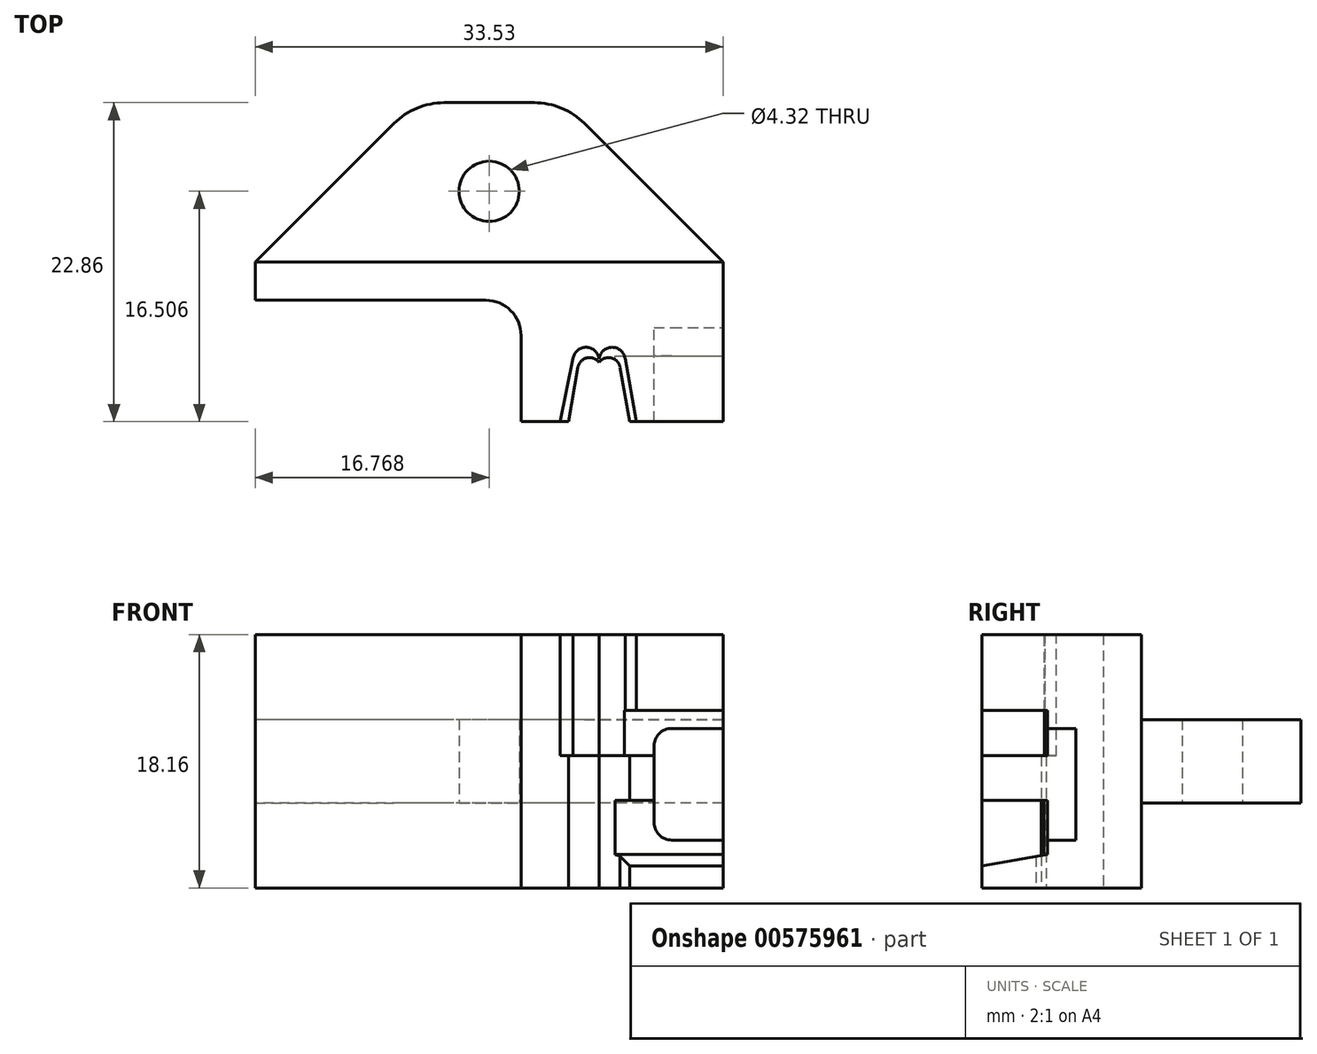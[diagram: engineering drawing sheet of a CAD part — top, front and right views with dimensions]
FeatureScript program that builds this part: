
annotation { "Feature Type Name" : "Feature", "Feature Type Description" : "" }
export const myFeature = defineFeature(function(context is Context, id is Id, definition is map)
    precondition{}
    {
        {
            var Q0;
            Q0=qCreatedBy(makeId("Top.planeOp"),FACE);
            var sketch = newSketch(context, id + "F0", { "sketchPlane" : qUnion([Q0])});
            skLineSegment(sketch, "E0.bottom", {"start": v(-12.43, 17.35) * mm, "end": v(21.1, 17.35) * mm});
            skLineSegment(sketch, "E0.top", {"start": v(-12.43, 5.92) * mm, "end": v(21.1, 5.92) * mm});
            skLineSegment(sketch, "E0.left", {"start": v(-12.43, 17.35) * mm, "end": v(-12.43, 5.92) * mm});
            skLineSegment(sketch, "E0.right", {"start": v(21.1, 17.35) * mm, "end": v(21.1, 5.92) * mm});
            skLineSegment(sketch, "E1.bottom", {"start": v(6.62, 5.92) * mm, "end": v(-9.89, 5.92) * mm});
            skLineSegment(sketch, "E1.top", {"start": v(6.62, 12.27) * mm, "end": v(-9.89, 12.27) * mm});
            skLineSegment(sketch, "E1.left", {"start": v(6.62, 5.92) * mm, "end": v(6.62, 12.27) * mm});
            skLineSegment(sketch, "E1.right", {"start": v(-9.89, 5.92) * mm, "end": v(-9.89, 12.27) * mm});
            skSolve(sketch);
        }
        {
            var Q0;
            Q0=makeQuery(id+"F0.imprint","IMPRINT",FACE,{"disambiguationData":[TD([[makeQuery(id+"F0.imprint","IMPRINT",EDGE,{"derivedFrom":sQuery(id+"F0.wireOp",EDGE,"E0.bottom")}),-1.0]])]});
            extrude(context, id + "F1", {"entities" : qUnion([Q0]), "depth" : 16.38 * mm, "offsetDistance" : 25.4 * mm});
        }
        {
            var Q0;
            Q0=makeQuery(id+"F1.opExtrude","SWEPT_FACE",FACE,{"disambiguationData":[OSD([sQuery(id+"F0.wireOp",EDGE,"E0.bottom")])]});
            var sketch = newSketch(context, id + "F2", { "sketchPlane" : qUnion([Q0])});
            skLineSegment(sketch, "E2.bottom", {"start": v(-21.1, 11.18) * mm, "end": v(12.43, 11.18) * mm});
            skLineSegment(sketch, "E2.top", {"start": v(-21.1, 5.2) * mm, "end": v(12.43, 5.2) * mm});
            skLineSegment(sketch, "E2.left", {"start": v(-21.1, 11.18) * mm, "end": v(-21.1, 5.2) * mm});
            skLineSegment(sketch, "E2.right", {"start": v(12.43, 11.18) * mm, "end": v(12.43, 5.2) * mm});
            skSolve(sketch);
        }
        {
            var Q0;
            Q0=makeQuery(id+"F2.imprint","IMPRINT",FACE,{"disambiguationData":[TD([[makeQuery(id+"F2.imprint","IMPRINT",EDGE,{"derivedFrom":sQuery(id+"F2.wireOp",EDGE,"E2.bottom")}),-1.0]])]});
            extrude(context, id + "F3", {"entities" : qUnion([Q0]), "operationType" : NewBodyOperationType.ADD, "depth" : 11.43 * mm, "offsetDistance" : 25.4 * mm});
        }
        {
            var Q0;
            Q0=makeQuery(id+"F3.opExtrude","CAP_EDGE",EDGE,{"disambiguationData":[OSD([sQuery(id+"F2.wireOp",EDGE,"E2.right")])],"isStart":false});
            var Q1;
            Q1=makeQuery(id+"F3.opExtrude","CAP_EDGE",EDGE,{"disambiguationData":[OSD([sQuery(id+"F2.wireOp",EDGE,"E2.left")])],"isStart":false});
            chamfer(context, id + "F4", {"entities" : qUnion([Q0, Q1]), "width" : 11.43 * mm, "tangentPropagation" : true});
        }
        {
            var Q0;
            Q0=makeQuery(id+"F3.opExtrude","SWEPT_FACE",FACE,{"disambiguationData":[OSD([sQuery(id+"F2.wireOp",EDGE,"E2.top")])]});
            var sketch = newSketch(context, id + "F5", { "sketchPlane" : qUnion([Q0])});
            skCircle(sketch, "E3", {"center": v(4.34, -22.43) * mm, "radius": 2.16 * mm});
            skSolve(sketch);
        }
        {
            var Q0;
            Q0=makeQuery(id+"F5.imprint","IMPRINT",FACE,{"disambiguationData":[TD([[makeQuery(id+"F5.imprint","IMPRINT",EDGE,{"derivedFrom":sQuery(id+"F5.wireOp",EDGE,"E3")}),1.0]])]});
            extrude(context, id + "F6", {"entities" : qUnion([Q0]), "operationType" : NewBodyOperationType.REMOVE, "oppositeDirection" : true, "depth" : 25.4 * mm, "offsetDistance" : 25.4 * mm});
        }
        {
            var Q0;
            Q0=makeQuery(id+"F1.opExtrude","CAP_FACE",FACE,{"disambiguationData":[OSD([sQuery(id+"F0.wireOp",EDGE,"E0.bottom"),sQuery(id+"F0.wireOp",EDGE,"E0.top"),sQuery(id+"F0.wireOp",EDGE,"E0.left"),sQuery(id+"F0.wireOp",EDGE,"E0.right")])],"isStart":true});
            var sketch = newSketch(context, id + "F7", { "sketchPlane" : qUnion([Q0])});
            skLineSegment(sketch, "E4", {"start": v(10.02, -5.92) * mm, "end": v(14.4, -5.92) * mm});
            skArc(sketch, "E5", {"start": v(12.21, -10.17) * mm, "mid": v(13.08, -10.5) * mm, "end": v(13.72, -9.82) * mm});
            skArc(sketch, "E6", {"start": v(10.7, -9.82) * mm, "mid": v(11.35, -10.5) * mm, "end": v(12.21, -10.17) * mm});
            skLineSegment(sketch, "E7", {"start": v(10.02, -5.92) * mm, "end": v(10.7, -9.82) * mm});
            skLineSegment(sketch, "E8", {"start": v(14.4, -5.92) * mm, "end": v(13.72, -9.82) * mm});
            skSolve(sketch);
        }
        {
            var Q0;
            Q0=makeQuery(id+"F7.imprint","IMPRINT",FACE,{"disambiguationData":[TD([[makeQuery(id+"F7.imprint","IMPRINT",EDGE,{"derivedFrom":sQuery(id+"F7.wireOp",EDGE,"E4")}),-1.0]])]});
            extrude(context, id + "F8", {"entities" : qUnion([Q0]), "operationType" : NewBodyOperationType.REMOVE, "oppositeDirection" : true, "depth" : 12.06 * mm, "offsetDistance" : 25.4 * mm});
        }
        {
            var Q0;
            Q0=makeQuery(id+"F1.opExtrude","CAP_FACE",FACE,{"disambiguationData":[OSD([sQuery(id+"F0.wireOp",EDGE,"E0.bottom"),sQuery(id+"F0.wireOp",EDGE,"E0.top"),sQuery(id+"F0.wireOp",EDGE,"E0.left"),sQuery(id+"F0.wireOp",EDGE,"E0.right")])],"isStart":false});
            var sketch = newSketch(context, id + "F9", { "sketchPlane" : qUnion([Q0])});
            skLineSegment(sketch, "E9", {"start": v(9.42, 5.92) * mm, "end": v(14.88, 5.92) * mm});
            skArc(sketch, "E10", {"start": v(12.21, 10.4) * mm, "mid": v(11.32, 11.25) * mm, "end": v(10.35, 10.47) * mm});
            skArc(sketch, "E11", {"start": v(14.08, 10.43) * mm, "mid": v(13.13, 11.25) * mm, "end": v(12.21, 10.4) * mm});
            skPoint(sketch, "E12.orphan", {"position": v(12.21, 10.23) * mm});
            skLineSegment(sketch, "E13", {"start": v(10.35, 10.47) * mm, "end": v(9.42, 5.92) * mm});
            skLineSegment(sketch, "E14", {"start": v(14.08, 10.43) * mm, "end": v(14.88, 5.92) * mm});
            skSolve(sketch);
        }
        {
            var Q0;
            Q0=makeQuery(id+"F9.imprint","IMPRINT",FACE,{"disambiguationData":[TD([[makeQuery(id+"F9.imprint","IMPRINT",EDGE,{"derivedFrom":sQuery(id+"F9.wireOp",EDGE,"E9")}),1.0]])]});
            extrude(context, id + "F10", {"entities" : qUnion([Q0]), "operationType" : NewBodyOperationType.REMOVE, "oppositeDirection" : true, "depth" : 7.8 * mm, "offsetDistance" : 25.4 * mm});
        }
        {
            var Q0;
            Q0=makeQuery(id+"F1.opExtrude","SWEPT_EDGE",EDGE,{"disambiguationData":[OSD([sQuery(id+"F0.wireOp",EDGE,"E1.top"),sQuery(id+"F0.wireOp",EDGE,"E1.left")])]});
            var Q1;
            Q1=makeQuery(id+"F1.opExtrude","SWEPT_EDGE",EDGE,{"disambiguationData":[OSD([sQuery(id+"F0.wireOp",EDGE,"E1.top"),sQuery(id+"F0.wireOp",EDGE,"E1.right")])]});
            fillet(context, id + "F11", {"entities" : qUnion([Q0, Q1]), "radius" : 6.35 * mm, "tangentPropagation" : true, "allowEdgeOverflow" : false});
        }
        {
            var Q0;
            Q0=makeQuery(id+"F3.boolean.opBoolean","MERGE",FACE,{"derivedFrom":[makeQuery(id+"F1.opExtrude","SWEPT_FACE",FACE,{"disambiguationData":[OSD([sQuery(id+"F0.wireOp",EDGE,"E0.right")])]}),makeQuery(id+"F3.opExtrude","SWEPT_FACE",FACE,{"disambiguationData":[OSD([sQuery(id+"F2.wireOp",EDGE,"E2.left")])]})]});
            var sketch = newSketch(context, id + "F12", { "sketchPlane" : qUnion([Q0])});
            skLineSegment(sketch, "E15.bottom", {"start": v(5.92, 0) * mm, "end": v(10.61, 0) * mm});
            skLineSegment(sketch, "E15.top", {"start": v(5.92, 5.4) * mm, "end": v(10.61, 5.4) * mm});
            skLineSegment(sketch, "E15.left", {"start": v(5.92, 0) * mm, "end": v(5.92, 5.4) * mm});
            skLineSegment(sketch, "E15.right", {"start": v(10.61, 0) * mm, "end": v(10.61, 5.4) * mm});
            skLineSegment(sketch, "E16.bottom", {"start": v(5.92, 8.59) * mm, "end": v(10.61, 8.59) * mm});
            skLineSegment(sketch, "E16.top", {"start": v(5.92, 11.82) * mm, "end": v(10.61, 11.82) * mm});
            skLineSegment(sketch, "E16.left", {"start": v(5.92, 8.59) * mm, "end": v(5.92, 11.82) * mm});
            skLineSegment(sketch, "E16.right", {"start": v(10.61, 8.59) * mm, "end": v(10.61, 11.82) * mm});
            skSolve(sketch);
        }
        {
            var Q0;
            Q0=makeQuery(id+"F12.imprint","IMPRINT",FACE,{"disambiguationData":[TD([[makeQuery(id+"F12.imprint","IMPRINT",EDGE,{"derivedFrom":sQuery(id+"F12.wireOp",EDGE,"E16.bottom")}),1.0]])]});
            var Q1;
            Q1=makeQuery(id+"F12.imprint","IMPRINT",FACE,{"disambiguationData":[TD([[makeQuery(id+"F12.imprint","IMPRINT",EDGE,{"derivedFrom":sQuery(id+"F12.wireOp",EDGE,"E15.bottom")}),-1.0]])]});
            extrude(context, id + "F13", {"entities" : qUnion([Q0, Q1]), "operationType" : NewBodyOperationType.REMOVE, "oppositeDirection" : true, "depth" : 7.75 * mm, "offsetDistance" : 25.4 * mm});
        }
        {
            var Q0;
            {var subQ0=sQuery(id+"F2.wireOp",EDGE,"E2.left");Q0=makeQuery(id+"F4.opChamfer","BLEND_EDGE",EDGE,{"blendedFrom":[makeQuery(id+"F3.opExtrude","CAP_EDGE",EDGE,{"disambiguationData":[OSD([subQ0])],"isStart":false}),makeQuery(id+"F3.opExtrude","CAP_FACE",FACE,{"disambiguationData":[OSD([sQuery(id+"F2.wireOp",EDGE,"E2.bottom"),sQuery(id+"F2.wireOp",EDGE,"E2.top"),subQ0,sQuery(id+"F2.wireOp",EDGE,"E2.right")])],"isStart":false})],"blendedInto":[makeQuery(id+"F3.opExtrude","CAP_FACE",FACE,{"disambiguationData":[OSD([sQuery(id+"F2.wireOp",EDGE,"E2.bottom"),sQuery(id+"F2.wireOp",EDGE,"E2.top"),subQ0,sQuery(id+"F2.wireOp",EDGE,"E2.right")])],"isStart":false})]});}
            var Q1;
            {var subQ0=sQuery(id+"F2.wireOp",EDGE,"E2.right");Q1=makeQuery(id+"F4.opChamfer","BLEND_EDGE",EDGE,{"blendedFrom":[makeQuery(id+"F3.opExtrude","CAP_EDGE",EDGE,{"disambiguationData":[OSD([subQ0])],"isStart":false}),makeQuery(id+"F3.opExtrude","CAP_FACE",FACE,{"disambiguationData":[OSD([sQuery(id+"F2.wireOp",EDGE,"E2.bottom"),sQuery(id+"F2.wireOp",EDGE,"E2.top"),sQuery(id+"F2.wireOp",EDGE,"E2.left"),subQ0])],"isStart":false})],"blendedInto":[makeQuery(id+"F3.opExtrude","CAP_FACE",FACE,{"disambiguationData":[OSD([sQuery(id+"F2.wireOp",EDGE,"E2.bottom"),sQuery(id+"F2.wireOp",EDGE,"E2.top"),sQuery(id+"F2.wireOp",EDGE,"E2.left"),subQ0])],"isStart":false})]});}
            fillet(context, id + "F14", {"entities" : qUnion([Q0, Q1]), "radius" : 5.08 * mm, "tangentPropagation" : true, "allowEdgeOverflow" : false});
        }
        {
            var Q0;
            Q0=makeQuery(id+"F3.boolean.opBoolean","MERGE",FACE,{"derivedFrom":[makeQuery(id+"F1.opExtrude","SWEPT_FACE",FACE,{"disambiguationData":[OSD([sQuery(id+"F0.wireOp",EDGE,"E0.right")])]}),makeQuery(id+"F3.opExtrude","SWEPT_FACE",FACE,{"disambiguationData":[OSD([sQuery(id+"F2.wireOp",EDGE,"E2.left")])]})]});
            var sketch = newSketch(context, id + "F15", { "sketchPlane" : qUnion([Q0])});
            skLineSegment(sketch, "E17.bottom", {"start": v(5.92, 5.4) * mm, "end": v(10.61, 5.4) * mm});
            skLineSegment(sketch, "E17.top", {"start": v(5.92, 8.59) * mm, "end": v(10.61, 8.59) * mm});
            skLineSegment(sketch, "E17.left", {"start": v(5.92, 5.4) * mm, "end": v(5.92, 8.59) * mm});
            skLineSegment(sketch, "E17.right", {"start": v(10.61, 5.4) * mm, "end": v(10.61, 8.59) * mm});
            skSolve(sketch);
        }
        {
            var Q0;
            Q0 = qSketchRegion(id + "F15", true);
            extrude(context, id + "F16", {"entities" : qUnion([Q0]), "operationType" : NewBodyOperationType.REMOVE, "oppositeDirection" : true, "depth" : 4.95 * mm, "offsetDistance" : 25.4 * mm});
        }
        {
            var Q0;
            {var subQ0=sQuery(id+"F0.wireOp",EDGE,"E0.top");Q0=makeQuery(id+"F1.opExtrude","SWEPT_FACE",FACE,{"disambiguationData":[OSD([subQ0]),TDD([makeQuery(id+"F0.imprint","IMPRINT",EDGE,{"disambiguationData":[TD([[makeQuery(id+"F0.imprint","INTERSECT",VERTEX,{"derivedFrom":[subQ0,sQuery(id+"F0.wireOp",EDGE,"E0.left")]}),-1.0]])],"derivedFrom":subQ0})])]});}
            var sketch = newSketch(context, id + "F17", { "sketchPlane" : qUnion([Q0])});
            skLineSegment(sketch, "E18.bottom", {"start": v(-12.43, 0) * mm, "end": v(-8.32, 0) * mm});
            skLineSegment(sketch, "E18.top", {"start": v(-12.43, 16.38) * mm, "end": v(-8.32, 16.38) * mm});
            skLineSegment(sketch, "E18.left", {"start": v(-12.43, 0) * mm, "end": v(-12.43, 16.38) * mm});
            skLineSegment(sketch, "E18.right", {"start": v(-8.32, 0) * mm, "end": v(-8.32, 16.38) * mm});
            skSolve(sketch);
        }
        {
            var Q0;
            {var subQ0=sQuery(id+"F17.wireOp",EDGE,"E18.left");Q0=makeQuery(id+"F17.imprint","IMPRINT",FACE,{"disambiguationData":[TD([[makeQuery(id+"F17.imprint","IMPRINT",EDGE,{"derivedFrom":subQ0}),1.0]])]});}
            var Q1;
            {var subQ4=sQuery(id+"F17.wireOp",EDGE,"E18.right");Q1=makeQuery(id+"F17.imprint","IMPRINT",FACE,{"disambiguationData":[TD([[makeQuery(id+"F17.imprint","IMPRINT",EDGE,{"derivedFrom":subQ4}),1.0]])]});}
            extrude(context, id + "F18", {"entities" : qUnion([Q0, Q1]), "operationType" : NewBodyOperationType.REMOVE, "oppositeDirection" : true, "depth" : 3.17 * mm, "offsetDistance" : 25.4 * mm});
        }
        {
            var Q0;
            Q0=makeQuery(id+"F3.boolean.opBoolean","MERGE",FACE,{"derivedFrom":[makeQuery(id+"F1.opExtrude","SWEPT_FACE",FACE,{"disambiguationData":[OSD([sQuery(id+"F0.wireOp",EDGE,"E0.right")])]}),makeQuery(id+"F3.opExtrude","SWEPT_FACE",FACE,{"disambiguationData":[OSD([sQuery(id+"F2.wireOp",EDGE,"E2.left")])]})]});
            var sketch = newSketch(context, id + "F19", { "sketchPlane" : qUnion([Q0])});
            skLineSegment(sketch, "E19.bottom", {"start": v(10.61, 10.54) * mm, "end": v(12.65, 10.54) * mm});
            skLineSegment(sketch, "E19.top", {"start": v(10.61, 2.54) * mm, "end": v(12.65, 2.54) * mm});
            skLineSegment(sketch, "E19.left", {"start": v(10.61, 10.54) * mm, "end": v(10.61, 2.54) * mm});
            skLineSegment(sketch, "E19.right", {"start": v(12.65, 10.54) * mm, "end": v(12.65, 2.54) * mm});
            skSolve(sketch);
        }
        {
            var Q0;
            Q0=makeQuery(id+"F19.imprint","IMPRINT",FACE,{"disambiguationData":[TD([[makeQuery(id+"F19.imprint","IMPRINT",EDGE,{"derivedFrom":sQuery(id+"F19.wireOp",EDGE,"E19.bottom")}),-1.0]])]});
            extrude(context, id + "F20", {"entities" : qUnion([Q0]), "operationType" : NewBodyOperationType.REMOVE, "oppositeDirection" : true, "depth" : 4.95 * mm, "offsetDistance" : 25.4 * mm});
        }
        {
            var Q0;
            Q0=makeQuery(id+"F1.opExtrude","CAP_FACE",FACE,{"disambiguationData":[OSD([sQuery(id+"F0.wireOp",EDGE,"E0.bottom"),sQuery(id+"F0.wireOp",EDGE,"E0.top"),sQuery(id+"F0.wireOp",EDGE,"E0.left"),sQuery(id+"F0.wireOp",EDGE,"E0.right"),sQuery(id+"F0.wireOp",EDGE,"E1.top"),sQuery(id+"F0.wireOp",EDGE,"E1.left"),sQuery(id+"F0.wireOp",EDGE,"E1.right")])],"isStart":true});
            var sketch = newSketch(context, id + "F21", { "sketchPlane" : qUnion([Q0])});
            skLineSegment(sketch, "E20.bottom", {"start": v(6.62, -5.92) * mm, "end": v(-12.43, -5.92) * mm});
            skLineSegment(sketch, "E20.top", {"start": v(6.62, -14.62) * mm, "end": v(-12.43, -14.62) * mm});
            skLineSegment(sketch, "E20.left", {"start": v(6.62, -5.92) * mm, "end": v(6.62, -14.62) * mm});
            skLineSegment(sketch, "E20.right", {"start": v(-12.43, -5.92) * mm, "end": v(-12.43, -14.62) * mm});
            skSolve(sketch);
        }
        {
            var Q0;
            Q0 = qSketchRegion(id + "F21", true);
            extrude(context, id + "F22", {"entities" : qUnion([Q0]), "operationType" : NewBodyOperationType.REMOVE, "oppositeDirection" : true, "depth" : 25.4 * mm, "offsetDistance" : 25.4 * mm});
        }
        {
            var Q0;
            Q0=makeQuery(id+"F22.boolean.opBoolean","COPY",EDGE,{"derivedFrom":makeQuery(id+"F22.opExtrude","SWEPT_EDGE",EDGE,{"disambiguationData":[OSD([sQuery(id+"F21.wireOp",EDGE,"E20.top"),sQuery(id+"F21.wireOp",EDGE,"E20.left")])]})});
            fillet(context, id + "F23", {"entities" : qUnion([Q0]), "radius" : 2.54 * mm, "tangentPropagation" : true, "allowEdgeOverflow" : false});
        }
        {
            var Q0;
            {var subQ1=sQuery(id+"F15.wireOp",EDGE,"E17.right");Q0=makeQuery(id+"F20.boolean.opBoolean","SPLIT",FACE,{"disambiguationData":[TD([makeQuery(id+"F13.boolean.opBoolean","COPY",FACE,{"derivedFrom":makeQuery(id+"F13.opExtrude","SWEPT_FACE",FACE,{"disambiguationData":[OSD([sQuery(id+"F12.wireOp",EDGE,"E15.top")])]})})])],"derivedFrom":makeQuery(id+"F16.boolean.opBoolean","MERGE",FACE,{"derivedFrom":[makeQuery(id+"F13.boolean.opBoolean","COPY",FACE,{"derivedFrom":makeQuery(id+"F13.opExtrude","SWEPT_FACE",FACE,{"disambiguationData":[OSD([sQuery(id+"F12.wireOp",EDGE,"E15.right")])]})}),makeQuery(id+"F13.boolean.opBoolean","COPY",FACE,{"derivedFrom":makeQuery(id+"F13.opExtrude","SWEPT_FACE",FACE,{"disambiguationData":[OSD([sQuery(id+"F12.wireOp",EDGE,"E16.right")])]})}),makeQuery(id+"F16.opExtrude","SWEPT_FACE",FACE,{"disambiguationData":[OSD([subQ1])]})]})});}
            var sketch = newSketch(context, id + "F24", { "sketchPlane" : qUnion([Q0])});
            skLineSegment(sketch, "E21.bottom", {"start": v(21.1, 0) * mm, "end": v(15.31, 0) * mm});
            skLineSegment(sketch, "E21.top", {"start": v(21.1, 2.6) * mm, "end": v(15.31, 2.6) * mm});
            skLineSegment(sketch, "E21.left", {"start": v(21.1, 0) * mm, "end": v(21.1, 2.6) * mm});
            skLineSegment(sketch, "E21.right", {"start": v(15.31, 0) * mm, "end": v(15.31, 2.6) * mm});
            skSolve(sketch);
        }
        {
            var Q0;
            Q0 = qSketchRegion(id + "F24", true);
            extrude(context, id + "F25", {"entities" : qUnion([Q0]), "operationType" : NewBodyOperationType.ADD, "depth" : 4.2 * mm, "offsetDistance" : 25.4 * mm});
        }
        {
            var Q0;
            Q0=makeQuery(id+"F25.boolean.opBoolean","MERGE",FACE,{"derivedFrom":[makeQuery(id+"F3.boolean.opBoolean","MERGE",FACE,{"derivedFrom":[makeQuery(id+"F1.opExtrude","SWEPT_FACE",FACE,{"disambiguationData":[OSD([sQuery(id+"F0.wireOp",EDGE,"E0.right")])]}),makeQuery(id+"F3.opExtrude","SWEPT_FACE",FACE,{"disambiguationData":[OSD([sQuery(id+"F2.wireOp",EDGE,"E2.left")])]})]}),makeQuery(id+"F25.opExtrude","SWEPT_FACE",FACE,{"disambiguationData":[OSD([sQuery(id+"F24.wireOp",EDGE,"E21.left")])]})]});
            var sketch = newSketch(context, id + "F26", { "sketchPlane" : qUnion([Q0])});
            skLineSegment(sketch, "E22", {"start": v(9.25, 1.28) * mm, "end": v(6.42, 0.79) * mm});
            skPoint(sketch, "E23.left.start.orphan", {"position": v(6.42, 1.3) * mm});
            skLineSegment(sketch, "E24", {"start": v(6.42, 0.79) * mm, "end": v(10.61, 1.53) * mm});
            skPoint(sketch, "E25.right.end.orphan", {"position": v(10.61, 2.05) * mm});
            skLineSegment(sketch, "E26", {"start": v(10.61, 2.6) * mm, "end": v(6.42, 2.6) * mm});
            skLineSegment(sketch, "E27", {"start": v(6.42, 2.6) * mm, "end": v(6.42, 0.79) * mm});
            skLineSegment(sketch, "E28", {"start": v(10.61, 2.6) * mm, "end": v(10.61, 1.53) * mm});
            skSolve(sketch);
        }
        {
            var Q0;
            Q0 = qSketchRegion(id + "F26", true);
            var Q1;
            {var subQ1=sQuery(id+"F26.wireOp",EDGE,"AyMfsVA2-HhfQ-rxy4-Jf4P-8pIKr9PG5E7d");Q1=makeQuery(id+"F26.imprint","IMPRINT",FACE,{"disambiguationData":[TD([[makeQuery(id+"F26.imprint","IMPRINT",EDGE,{"derivedFrom":subQ1}),1.0]])]});}
            var Q2;
            {var subQ1=sQuery(id+"F26.wireOp",EDGE,"E22");Q2=makeQuery(id+"F26.imprint","IMPRINT",FACE,{"disambiguationData":[TD([[makeQuery(id+"F26.imprint","IMPRINT",EDGE,{"derivedFrom":subQ1}),-1.0]])]});}
            extrude(context, id + "F27", {"entities" : qUnion([Q0, Q1, Q2]), "operationType" : NewBodyOperationType.REMOVE, "oppositeDirection" : true, "depth" : 6.27 * mm, "offsetDistance" : 25.4 * mm});
        }
        {
            var Q0;
            Q0=makeQuery(id+"F20.boolean.opBoolean","COPY",EDGE,{"derivedFrom":makeQuery(id+"F20.opExtrude","CAP_EDGE",EDGE,{"disambiguationData":[OSD([sQuery(id+"F19.wireOp",EDGE,"E19.bottom")])],"isStart":false})});
            var Q1;
            Q1=makeQuery(id+"F20.boolean.opBoolean","COPY",EDGE,{"derivedFrom":makeQuery(id+"F20.opExtrude","CAP_EDGE",EDGE,{"disambiguationData":[OSD([sQuery(id+"F19.wireOp",EDGE,"E19.top")])],"isStart":false})});
            fillet(context, id + "F28", {"entities" : qUnion([Q0, Q1]), "radius" : 1.27 * mm, "tangentPropagation" : true, "allowEdgeOverflow" : false});
        }
        {
            var Q0;
            Q0=makeQuery(id+"F1.opExtrude","CAP_FACE",FACE,{"disambiguationData":[OSD([sQuery(id+"F0.wireOp",EDGE,"E0.bottom"),sQuery(id+"F0.wireOp",EDGE,"E0.top"),sQuery(id+"F0.wireOp",EDGE,"E0.left"),sQuery(id+"F0.wireOp",EDGE,"E0.right"),sQuery(id+"F0.wireOp",EDGE,"E1.top"),sQuery(id+"F0.wireOp",EDGE,"E1.left"),sQuery(id+"F0.wireOp",EDGE,"E1.right")])],"isStart":false});
            var sketch = newSketch(context, id + "F29", { "sketchPlane" : qUnion([Q0])});
            skLineSegment(sketch, "E29.bottom", {"start": v(-12.43, 17.35) * mm, "end": v(21.1, 17.35) * mm});
            skLineSegment(sketch, "E29.top", {"start": v(6.62, 5.92) * mm, "end": v(9.42, 5.92) * mm});
            skLineSegment(sketch, "E29.left", {"start": v(-12.43, 17.35) * mm, "end": v(-12.43, 5.92) * mm});
            skLineSegment(sketch, "E29.right", {"start": v(21.1, 17.35) * mm, "end": v(21.1, 5.92) * mm});
            skArc(sketch, "E30", {"start": v(6.62, 12.08) * mm, "mid": v(5.88, 13.88) * mm, "end": v(4.08, 14.62) * mm});
            skLineSegment(sketch, "E31", {"start": v(-12.43, 14.62) * mm, "end": v(4.08, 14.62) * mm});
            skLineSegment(sketch, "E32", {"start": v(6.62, 12.08) * mm, "end": v(6.62, 5.92) * mm});
            skLineSegment(sketch, "E33", {"start": v(14.08, 10.43) * mm, "end": v(14.88, 5.92) * mm});
            skLineSegment(sketch, "E34", {"start": v(10.35, 10.47) * mm, "end": v(9.42, 5.92) * mm});
            skArc(sketch, "E35", {"start": v(12.21, 10.4) * mm, "mid": v(11.32, 11.25) * mm, "end": v(10.35, 10.47) * mm});
            skArc(sketch, "E36", {"start": v(14.08, 10.43) * mm, "mid": v(13.13, 11.25) * mm, "end": v(12.21, 10.4) * mm});
            skLineSegment(sketch, "E37.trimOffspring", {"start": v(14.88, 5.92) * mm, "end": v(21.1, 5.92) * mm});
            skSolve(sketch);
        }
        {
            var Q0;
            Q0 = qSketchRegion(id + "F29", true);
            extrude(context, id + "F30", {"entities" : qUnion([Q0]), "operationType" : NewBodyOperationType.ADD, "depth" : 0.89 * mm, "offsetDistance" : 25.4 * mm});
        }
        {
            var Q0;
            Q0=makeQuery(id+"F25.boolean.opBoolean","MERGE",FACE,{"derivedFrom":[makeQuery(id+"F1.opExtrude","CAP_FACE",FACE,{"disambiguationData":[OSD([sQuery(id+"F0.wireOp",EDGE,"E0.bottom"),sQuery(id+"F0.wireOp",EDGE,"E0.top"),sQuery(id+"F0.wireOp",EDGE,"E0.left"),sQuery(id+"F0.wireOp",EDGE,"E0.right"),sQuery(id+"F0.wireOp",EDGE,"E1.top"),sQuery(id+"F0.wireOp",EDGE,"E1.left"),sQuery(id+"F0.wireOp",EDGE,"E1.right")])],"isStart":true}),makeQuery(id+"F25.opExtrude","SWEPT_FACE",FACE,{"disambiguationData":[OSD([sQuery(id+"F24.wireOp",EDGE,"E21.bottom")])]})]});
            var sketch = newSketch(context, id + "F31", { "sketchPlane" : qUnion([Q0])});
            skLineSegment(sketch, "E38.bottom", {"start": v(-12.43, -17.35) * mm, "end": v(21.1, -17.35) * mm});
            skLineSegment(sketch, "E38.top", {"start": v(6.62, -5.92) * mm, "end": v(10.02, -5.92) * mm});
            skLineSegment(sketch, "E38.left", {"start": v(-12.43, -17.35) * mm, "end": v(-12.43, -14.62) * mm});
            skLineSegment(sketch, "E38.right", {"start": v(21.1, -17.35) * mm, "end": v(21.1, -6.42) * mm});
            skArc(sketch, "E39", {"start": v(4.08, -14.62) * mm, "mid": v(5.88, -13.88) * mm, "end": v(6.62, -12.08) * mm});
            skArc(sketch, "E40", {"start": v(10.7, -9.82) * mm, "mid": v(11.35, -10.5) * mm, "end": v(12.21, -10.17) * mm});
            skArc(sketch, "E41", {"start": v(12.21, -10.17) * mm, "mid": v(12.74, -10.5) * mm, "end": v(13.36, -10.37) * mm});
            skLineSegment(sketch, "E42", {"start": v(-12.43, -14.62) * mm, "end": v(4.08, -14.62) * mm});
            skLineSegment(sketch, "E43", {"start": v(15.31, -10.37) * mm, "end": v(15.31, -6.42) * mm});
            skLineSegment(sketch, "E44", {"start": v(10.02, -5.92) * mm, "end": v(10.7, -9.82) * mm});
            skLineSegment(sketch, "E45", {"start": v(10.7, -9.82) * mm, "end": v(10.72, -9.67) * mm});
            skLineSegment(sketch, "E46", {"start": v(6.62, -5.92) * mm, "end": v(6.62, -12.08) * mm});
            skLineSegment(sketch, "E47.trimOffspring", {"start": v(15.31, -6.42) * mm, "end": v(21.1, -6.42) * mm});
            skLineSegment(sketch, "E48", {"start": v(13.36, -10.37) * mm, "end": v(15.31, -10.37) * mm});
            skSolve(sketch);
        }
        {
            var Q0;
            Q0 = qSketchRegion(id + "F31", true);
            extrude(context, id + "F32", {"entities" : qUnion([Q0]), "operationType" : NewBodyOperationType.ADD, "depth" : 0.89 * mm, "offsetDistance" : 25.4 * mm, "hasSecondDirection" : true, "secondDirectionOppositeDirection" : true, "secondDirectionDepth" : 0.71 * mm});
        }
        {
            var Q0;
            Q0=makeQuery(id+"F32.boolean.opBoolean","MERGE",FACE,{"derivedFrom":[makeQuery(id+"F30.boolean.opBoolean","MERGE",FACE,{"derivedFrom":[makeQuery(id+"FNT10bEfAjoNqos_1.boolean.opBoolean","MERGE",FACE,{"derivedFrom":[makeQuery(id+"F25.boolean.opBoolean","MERGE",FACE,{"derivedFrom":[makeQuery(id+"F3.boolean.opBoolean","MERGE",FACE,{"derivedFrom":[makeQuery(id+"F1.opExtrude","SWEPT_FACE",FACE,{"disambiguationData":[OSD([sQuery(id+"F0.wireOp",EDGE,"E0.right")])]}),makeQuery(id+"F3.opExtrude","SWEPT_FACE",FACE,{"disambiguationData":[OSD([sQuery(id+"F2.wireOp",EDGE,"E2.left")])]})]}),makeQuery(id+"F25.opExtrude","SWEPT_FACE",FACE,{"disambiguationData":[OSD([sQuery(id+"F24.wireOp",EDGE,"E21.left")])]})]}),makeQuery(id+"FNT10bEfAjoNqos_1.opExtrude","CAP_FACE",FACE,{"disambiguationData":[OSD([sQuery(id+"FU6olysg6OqCnIC_1.wireOp",EDGE,"qaEkds9a-dSHN-xRgu-P83B-4xmxqSmt1G8P"),sQuery(id+"FU6olysg6OqCnIC_1.wireOp",EDGE,"y9xs4YRf-jjso-odQC-tZ7Q-1LSNoCF4wCtS"),sQuery(id+"FU6olysg6OqCnIC_1.wireOp",EDGE,"yXoEhX52-ssEP-JOF9-UMfl-Un6ATPNGeLj2")])],"isStart":true})]}),makeQuery(id+"F30.opExtrude","SWEPT_FACE",FACE,{"disambiguationData":[OSD([sQuery(id+"F29.wireOp",EDGE,"E29.right")])]})]}),makeQuery(id+"F32.opExtrude","SWEPT_FACE",FACE,{"disambiguationData":[OSD([sQuery(id+"F31.wireOp",EDGE,"E38.right")])]})]});
            var sketch = newSketch(context, id + "F33", { "sketchPlane" : qUnion([Q0])});
            skLineSegment(sketch, "E49.bottom", {"start": v(5.92, 11.82) * mm, "end": v(10.61, 11.82) * mm});
            skLineSegment(sketch, "E49.top", {"start": v(5.92, 10.54) * mm, "end": v(10.61, 10.54) * mm});
            skLineSegment(sketch, "E49.left", {"start": v(5.92, 10.54) * mm, "end": v(5.92, 11.82) * mm});
            skLineSegment(sketch, "E49.right", {"start": v(10.61, 10.54) * mm, "end": v(10.61, 11.82) * mm});
            skSolve(sketch);
        }
        {
            var Q0;
            Q0 = qSketchRegion(id + "F33", true);
            extrude(context, id + "F34", {"entities" : qUnion([Q0]), "operationType" : NewBodyOperationType.REMOVE, "oppositeDirection" : true, "depth" : 7.77 * mm, "offsetDistance" : 25.4 * mm});
        }
        {
            var Q0;
            Q0=makeQuery(id+"F32.boolean.opBoolean","MERGE",FACE,{"derivedFrom":[makeQuery(id+"F25.opExtrude","SWEPT_FACE",FACE,{"disambiguationData":[OSD([sQuery(id+"F24.wireOp",EDGE,"E21.right")])]}),makeQuery(id+"F32.opExtrude","SWEPT_FACE",FACE,{"disambiguationData":[OSD([sQuery(id+"F31.wireOp",EDGE,"E43")])]})]});
            var sketch = newSketch(context, id + "F35", { "sketchPlane" : qUnion([Q0])});
            skLineSegment(sketch, "E50", {"start": v(-10.37, -0.89) * mm, "end": v(-10.37, 0.71) * mm});
            skLineSegment(sketch, "E51", {"start": v(-10.37, 0.71) * mm, "end": v(-10.61, 0.71) * mm});
            skLineSegment(sketch, "E52", {"start": v(-10.61, 1.53) * mm, "end": v(-6.42, 0.79) * mm});
            skLineSegment(sketch, "E53", {"start": v(-6.42, 0.79) * mm, "end": v(-6.42, -0.89) * mm});
            skLineSegment(sketch, "E54", {"start": v(-6.42, -0.89) * mm, "end": v(-6.52, -0.86) * mm});
            skLineSegment(sketch, "E55", {"start": v(-6.42, -0.89) * mm, "end": v(-10.37, -0.89) * mm});
            skLineSegment(sketch, "E56", {"start": v(-10.61, 0.71) * mm, "end": v(-10.61, 1.53) * mm});
            skSolve(sketch);
        }
        {
            var Q0;
            Q0 = qSketchRegion(id + "F35", true);
            extrude(context, id + "F36", {"entities" : qUnion([Q0]), "operationType" : NewBodyOperationType.ADD, "depth" : 1.96 * mm, "offsetDistance" : 25.4 * mm});
        }
        {
            var Q0;
            Q0=makeQuery(id+"F36.boolean.opBoolean","MERGE",FACE,{"derivedFrom":[makeQuery(id+"F32.opExtrude","CAP_FACE",FACE,{"disambiguationData":[OSD([sQuery(id+"F31.wireOp",EDGE,"E38.bottom"),sQuery(id+"F31.wireOp",EDGE,"E38.top"),sQuery(id+"F31.wireOp",EDGE,"E38.left"),sQuery(id+"F31.wireOp",EDGE,"E38.right"),sQuery(id+"F31.wireOp",EDGE,"E39"),sQuery(id+"F31.wireOp",EDGE,"E40"),sQuery(id+"F31.wireOp",EDGE,"E41"),sQuery(id+"F31.wireOp",EDGE,"E42"),sQuery(id+"F31.wireOp",EDGE,"E43"),sQuery(id+"F31.wireOp",EDGE,"E44"),sQuery(id+"F31.wireOp",EDGE,"E46"),sQuery(id+"F31.wireOp",EDGE,"E47.trimOffspring"),sQuery(id+"F31.wireOp",EDGE,"E48")])],"isStart":false}),makeQuery(id+"F36.opExtrude","SWEPT_FACE",FACE,{"disambiguationData":[OSD([sQuery(id+"F35.wireOp",EDGE,"E55")])]})]});
            var sketch = newSketch(context, id + "F37", { "sketchPlane" : qUnion([Q0])});
            skArc(sketch, "E57", {"start": v(13.36, -10.37) * mm, "mid": v(13.6, -10.13) * mm, "end": v(13.72, -9.8) * mm});
            skLineSegment(sketch, "E58", {"start": v(13.72, -9.8) * mm, "end": v(14.32, -6.42) * mm});
            skPoint(sketch, "E59.center.orphan", {"position": v(11.53, -9.68) * mm});
            skLineSegment(sketch, "E60", {"start": v(14.32, -6.42) * mm, "end": v(13.36, -6.42) * mm});
            skLineSegment(sketch, "E61", {"start": v(13.36, -6.42) * mm, "end": v(13.36, -10.37) * mm});
            skSolve(sketch);
        }
        {
            var Q0;
            Q0 = qSketchRegion(id + "F37", true);
            extrude(context, id + "F38", {"entities" : qUnion([Q0]), "operationType" : NewBodyOperationType.REMOVE, "oppositeDirection" : true, "depth" : 25.4 * mm, "offsetDistance" : 25.4 * mm});
        }
        {
            var Q0;
            Q0=makeQuery(id+"F36.boolean.opBoolean","MERGE",FACE,{"derivedFrom":[makeQuery(id+"F32.opExtrude","CAP_FACE",FACE,{"disambiguationData":[OSD([sQuery(id+"F31.wireOp",EDGE,"E38.bottom"),sQuery(id+"F31.wireOp",EDGE,"E38.top"),sQuery(id+"F31.wireOp",EDGE,"E38.left"),sQuery(id+"F31.wireOp",EDGE,"E38.right"),sQuery(id+"F31.wireOp",EDGE,"E39"),sQuery(id+"F31.wireOp",EDGE,"E40"),sQuery(id+"F31.wireOp",EDGE,"E41"),sQuery(id+"F31.wireOp",EDGE,"E42"),sQuery(id+"F31.wireOp",EDGE,"E43"),sQuery(id+"F31.wireOp",EDGE,"E44"),sQuery(id+"F31.wireOp",EDGE,"E46"),sQuery(id+"F31.wireOp",EDGE,"E47.trimOffspring"),sQuery(id+"F31.wireOp",EDGE,"E48")])],"isStart":false}),makeQuery(id+"F36.opExtrude","SWEPT_FACE",FACE,{"disambiguationData":[OSD([sQuery(id+"F35.wireOp",EDGE,"E55")])]})]});
            var sketch = newSketch(context, id + "F39", { "sketchPlane" : qUnion([Q0])});
            skLineSegment(sketch, "E62.bottom", {"start": v(21.1, -6.42) * mm, "end": v(14.32, -6.42) * mm});
            skLineSegment(sketch, "E62.top", {"start": v(21.1, -5.92) * mm, "end": v(14.4, -5.92) * mm});
            skLineSegment(sketch, "E62.left", {"start": v(21.1, -6.42) * mm, "end": v(21.1, -5.92) * mm});
            skLineSegment(sketch, "E63", {"start": v(14.32, -6.42) * mm, "end": v(14.4, -5.92) * mm});
            skPoint(sketch, "E64.orphan", {"position": v(14.32, -5.92) * mm});
            skSolve(sketch);
        }
        {
            var Q0;
            Q0 = qSketchRegion(id + "F39", true);
            extrude(context, id + "F40", {"entities" : qUnion([Q0]), "operationType" : NewBodyOperationType.ADD, "oppositeDirection" : true, "depth" : 1.7 * mm, "offsetDistance" : 25.4 * mm});
        }
        {
            var Q0;
            Q0=makeQuery(id+"F40.boolean.opBoolean","MERGE",FACE,{"derivedFrom":[makeQuery(id+"F32.boolean.opBoolean","MERGE",FACE,{"derivedFrom":[makeQuery(id+"F30.boolean.opBoolean","MERGE",FACE,{"derivedFrom":[makeQuery(id+"F25.boolean.opBoolean","MERGE",FACE,{"derivedFrom":[makeQuery(id+"F3.boolean.opBoolean","MERGE",FACE,{"derivedFrom":[makeQuery(id+"F1.opExtrude","SWEPT_FACE",FACE,{"disambiguationData":[OSD([sQuery(id+"F0.wireOp",EDGE,"E0.right")])]}),makeQuery(id+"F3.opExtrude","SWEPT_FACE",FACE,{"disambiguationData":[OSD([sQuery(id+"F2.wireOp",EDGE,"E2.left")])]})]}),makeQuery(id+"F25.opExtrude","SWEPT_FACE",FACE,{"disambiguationData":[OSD([sQuery(id+"F24.wireOp",EDGE,"E21.left")])]})]}),makeQuery(id+"F30.opExtrude","SWEPT_FACE",FACE,{"disambiguationData":[OSD([sQuery(id+"F29.wireOp",EDGE,"E29.right")])]})]}),makeQuery(id+"F32.opExtrude","SWEPT_FACE",FACE,{"disambiguationData":[OSD([sQuery(id+"F31.wireOp",EDGE,"E38.right")])]})]}),makeQuery(id+"F40.opExtrude","SWEPT_FACE",FACE,{"disambiguationData":[OSD([sQuery(id+"F39.wireOp",EDGE,"E62.left")])]})]});
            var sketch = newSketch(context, id + "F41", { "sketchPlane" : qUnion([Q0])});
            skLineSegment(sketch, "E65", {"start": v(6.42, 0.79) * mm, "end": v(5.92, 0.7) * mm});
            skLineSegment(sketch, "E66", {"start": v(5.92, 0.7) * mm, "end": v(5.92, 0.82) * mm});
            skLineSegment(sketch, "E67", {"start": v(5.92, 0.82) * mm, "end": v(6.42, 0.82) * mm});
            skLineSegment(sketch, "E68", {"start": v(6.42, 0.82) * mm, "end": v(6.42, 0.79) * mm});
            skSolve(sketch);
        }
        {
            var Q0;
            Q0 = qSketchRegion(id + "F41", true);
            extrude(context, id + "F42", {"entities" : qUnion([Q0]), "operationType" : NewBodyOperationType.REMOVE, "oppositeDirection" : true, "depth" : 6.96 * mm, "offsetDistance" : 25.4 * mm});
        }
    });
